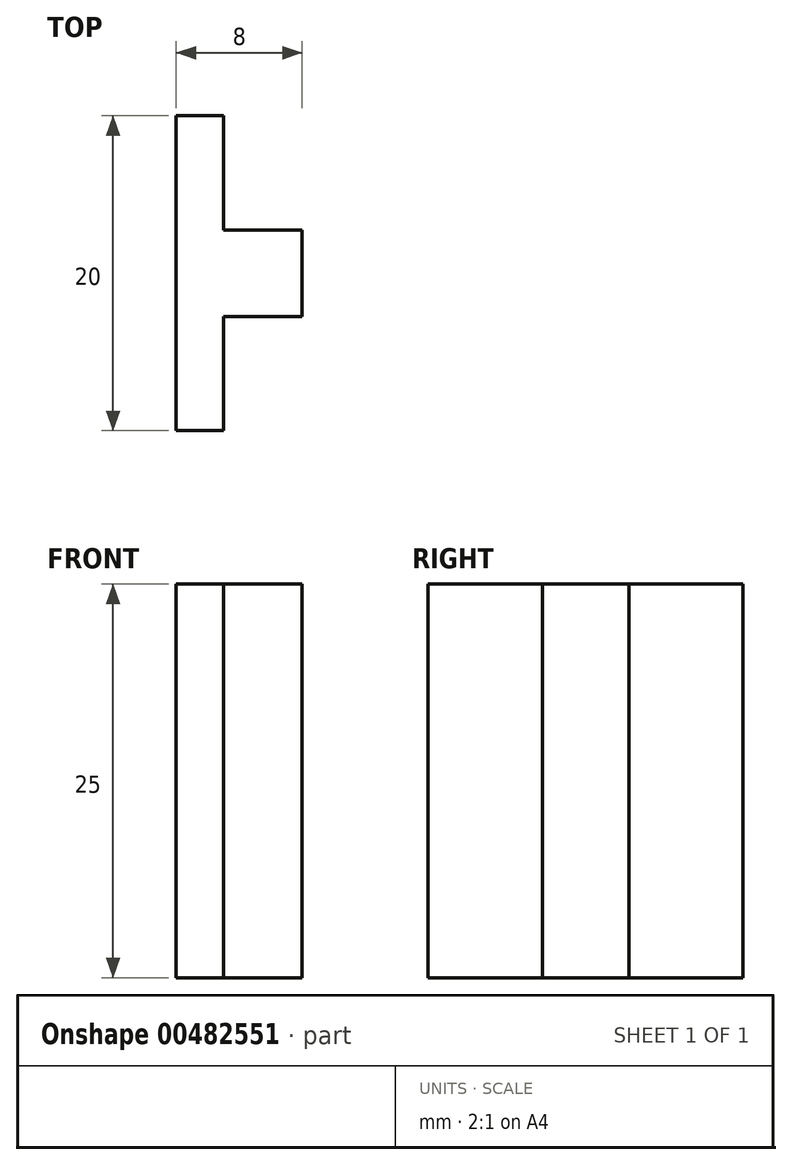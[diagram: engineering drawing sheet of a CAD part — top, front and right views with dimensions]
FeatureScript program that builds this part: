
annotation { "Feature Type Name" : "Feature", "Feature Type Description" : "" }
export const myFeature = defineFeature(function(context is Context, id is Id, definition is map)
    precondition{}
    {
        {
            var Q0;
            Q0=qCreatedBy(makeId("Top.planeOp"),FACE);
            var sketch = newSketch(context, id + "F0", { "sketchPlane" : qUnion([Q0])});
            skLineSegment(sketch, "E0.bottom", {"start": v(-5, 5.5) * mm, "end": v(0, 5.5) * mm});
            skLineSegment(sketch, "E0.top", {"start": v(-5, 0) * mm, "end": v(0, 0) * mm});
            skLineSegment(sketch, "E0.right", {"start": v(0, 5.5) * mm, "end": v(0, 0) * mm});
            skPoint(sketch, "E1", {"position": v(0, 0) * mm});
            skLineSegment(sketch, "E2.bottom", {"start": v(-5, -7.25) * mm, "end": v(-8, -7.25) * mm});
            skLineSegment(sketch, "E2.top", {"start": v(-5, 12.75) * mm, "end": v(-8, 12.75) * mm});
            skLineSegment(sketch, "E2.left", {"start": v(-5, -7.25) * mm, "end": v(-5, 0) * mm});
            skLineSegment(sketch, "E2.right", {"start": v(-8, -7.25) * mm, "end": v(-8, 12.75) * mm});
            skLineSegment(sketch, "E3", {"start": v(-5, 5.5) * mm, "end": v(-5, 12.75) * mm});
            skSolve(sketch);
        }
        {
            var Q0;
            Q0=makeQuery(id+"F0.imprint","IMPRINT",FACE,{"disambiguationData":[TD([[makeQuery(id+"F0.imprint","IMPRINT",EDGE,{"derivedFrom":sQuery(id+"F0.wireOp",EDGE,"E0.bottom")}),-1.0]])]});
            var sketch = newSketch(context, id + "F1", { "sketchPlane" : qUnion([Q0])});
            skSolve(sketch);
        }
        {
            var Q0;
            Q0=makeQuery(id+"F1.imprint","IMPRINT",FACE,{"disambiguationData":[TD([[makeQuery(id+"F1.imprint","IMPRINT",EDGE,{"derivedFrom":makeQuery(id+"F0.imprint","IMPRINT",EDGE,{"derivedFrom":sQuery(id+"F0.wireOp",EDGE,"E0.bottom")})}),-1.0]])]});
            extrude(context, id + "F2", {"entities" : qUnion([Q0]), "depth" : 25 * mm});
        }
    });
